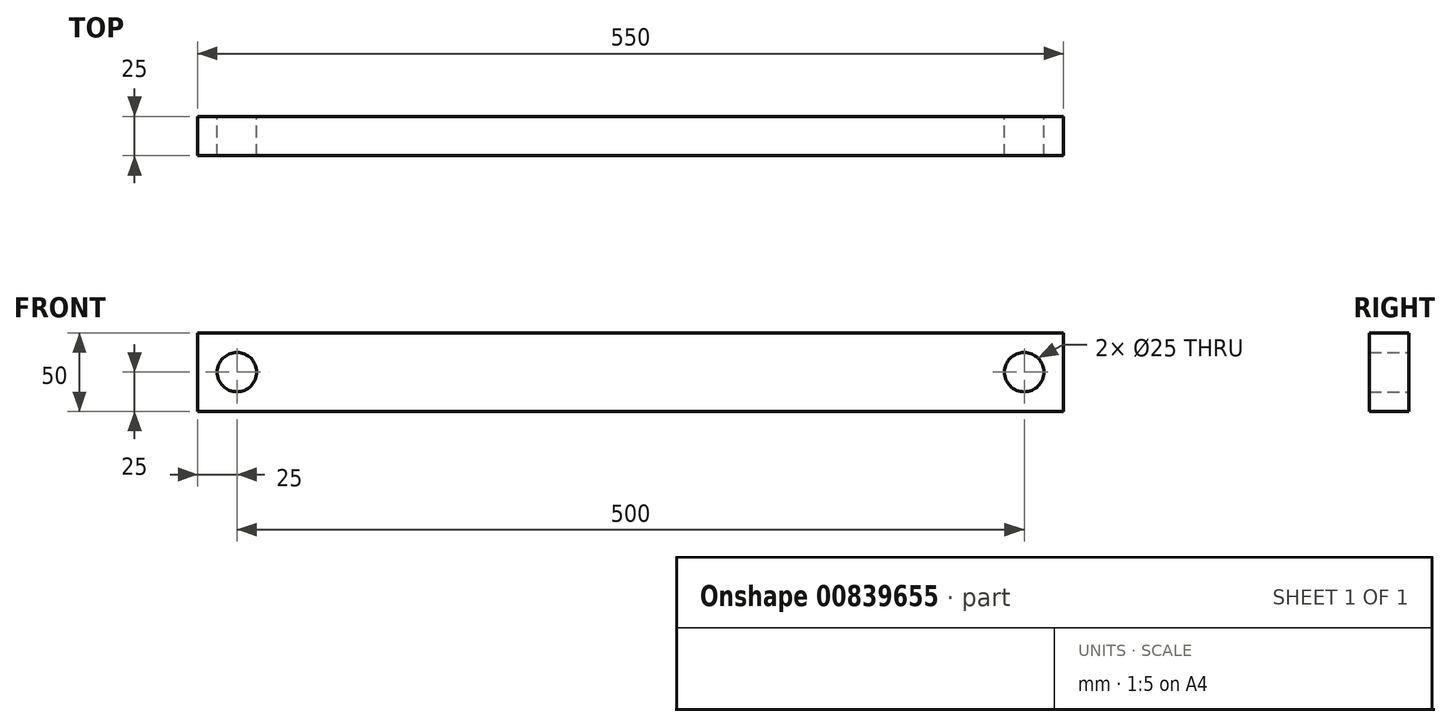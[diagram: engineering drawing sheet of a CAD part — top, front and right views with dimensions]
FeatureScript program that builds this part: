
annotation { "Feature Type Name" : "Feature", "Feature Type Description" : "" }
export const myFeature = defineFeature(function(context is Context, id is Id, definition is map)
    precondition{}
    {
        {
            var Q0;
            Q0=qCreatedBy(makeId("Front.planeOp"),FACE);
            var sketch = newSketch(context, id + "F0", { "sketchPlane" : qUnion([Q0])});
            skCircle(sketch, "E0", {"center": v(-250, 0) * mm, "radius": 12.5 * mm});
            skCircle(sketch, "E1", {"center": v(250, 0) * mm, "radius": 12.5 * mm});
            skLineSegment(sketch, "E2", {"start": v(-250, 0) * mm, "end": v(250, 0) * mm, "construction": true});
            skPoint(sketch, "E3", {"position": v(0, 0) * mm});
            skLineSegment(sketch, "E4.bottom", {"start": v(-275, 25) * mm, "end": v(275, 25) * mm});
            skLineSegment(sketch, "E4.top", {"start": v(-275, -25) * mm, "end": v(275, -25) * mm});
            skLineSegment(sketch, "E4.left", {"start": v(-275, 25) * mm, "end": v(-275, -25) * mm});
            skLineSegment(sketch, "E4.right", {"start": v(275, 25) * mm, "end": v(275, -25) * mm});
            skLineSegment(sketch, "E5", {"start": v(250, 0) * mm, "end": v(275, 25) * mm, "construction": true});
            skLineSegment(sketch, "E6", {"start": v(250, 0) * mm, "end": v(275, -25) * mm, "construction": true});
            skLineSegment(sketch, "E7", {"start": v(-250, 0) * mm, "end": v(-275, 25) * mm, "construction": true});
            skLineSegment(sketch, "E8", {"start": v(-250, 0) * mm, "end": v(-275, -25) * mm, "construction": true});
            skSolve(sketch);
        }
        {
            var Q0;
            Q0=makeQuery(id+"F0.imprint","IMPRINT",FACE,{"disambiguationData":[TD([[makeQuery(id+"F0.imprint","IMPRINT",EDGE,{"derivedFrom":sQuery(id+"F0.wireOp",EDGE,"E0")}),-1.0]])]});
            extrude(context, id + "F1", {"entities" : qUnion([Q0]), "depth" : 25 * mm, "offsetDistance" : 25 * mm});
        }
    });
